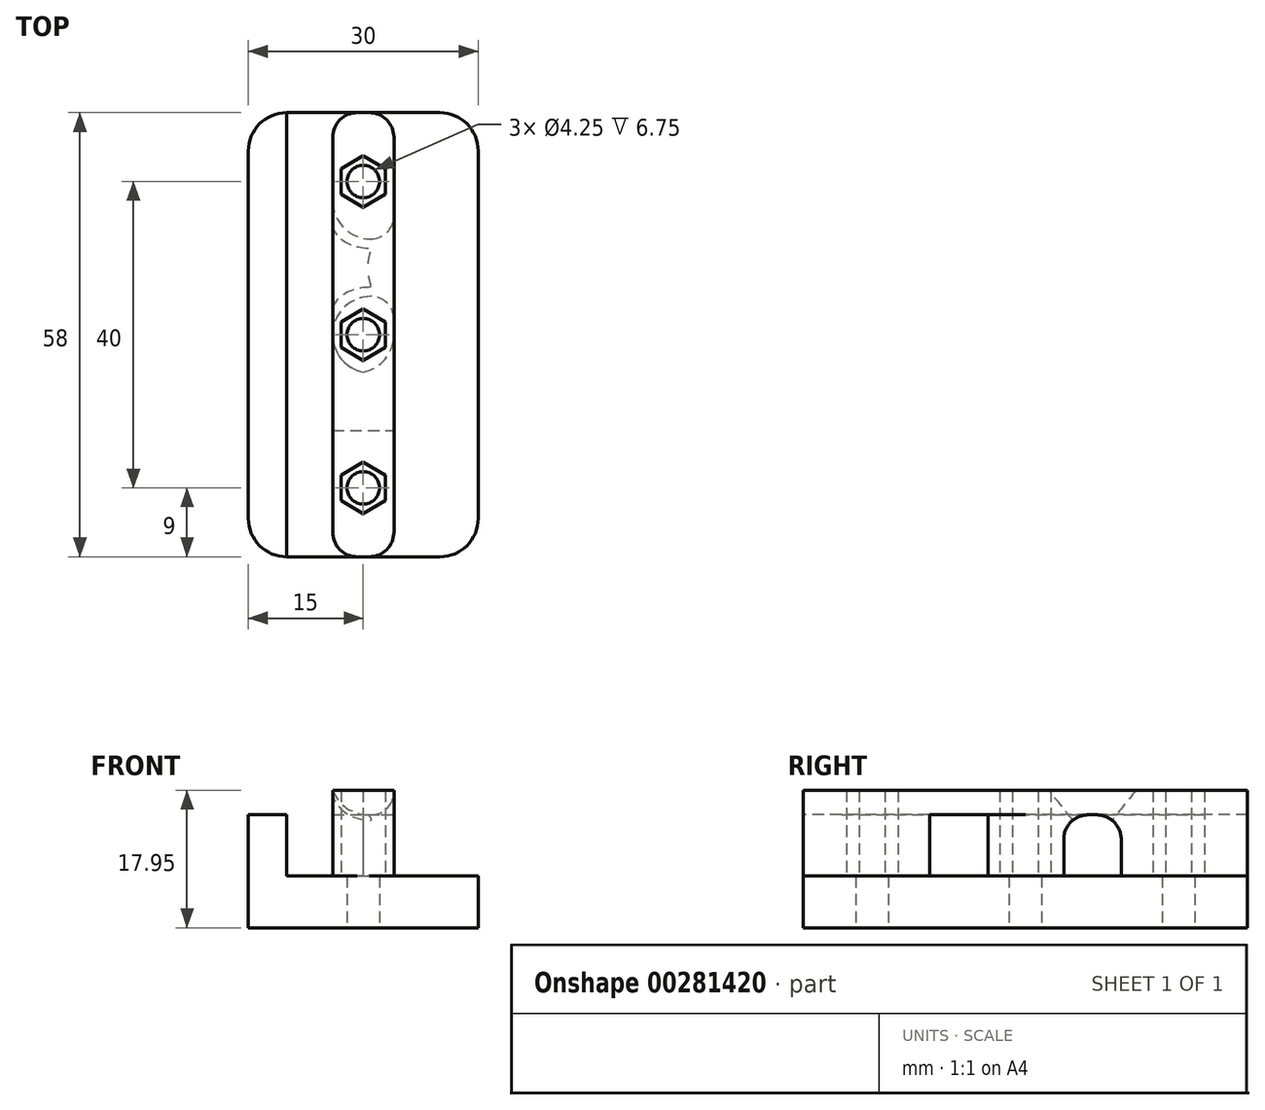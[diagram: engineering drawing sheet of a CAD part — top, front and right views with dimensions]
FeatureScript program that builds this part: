
annotation { "Feature Type Name" : "Feature", "Feature Type Description" : "" }
export const myFeature = defineFeature(function(context is Context, id is Id, definition is map)
    precondition{}
    {
        {
            var Q0;
            Q0=qCreatedBy(makeId("Top.planeOp"),FACE);
            var sketch = newSketch(context, id + "F0", { "sketchPlane" : qUnion([Q0])});
            skLineSegment(sketch, "E0.bottom", {"start": v(15, -29) * mm, "end": v(-15, -29) * mm});
            skLineSegment(sketch, "E0.top", {"start": v(15, 29) * mm, "end": v(-15, 29) * mm});
            skLineSegment(sketch, "E0.left", {"start": v(15, -29) * mm, "end": v(15, 29) * mm});
            skLineSegment(sketch, "E0.right", {"start": v(-15, -29) * mm, "end": v(-15, 29) * mm});
            skPoint(sketch, "E0.middle", {"position": v(0, 0) * mm});
            skCircle(sketch, "E1", {"center": v(0, 20) * mm, "radius": 2.12 * mm});
            skCircle(sketch, "E2", {"center": v(0, -20) * mm, "radius": 2.12 * mm});
            skCircle(sketch, "E3", {"center": v(0, 0) * mm, "radius": 2.12 * mm});
            skSolve(sketch);
        }
        {
            var Q0;
            Q0=qSketchRegion(id+"F0",true);
            extrude(context, id + "F1", {"entities" : qUnion([Q0]), "depth" : 6.75 * mm});
        }
        {
            var Q0;
            Q0=makeQuery(id+"F1.opExtrude","CAP_FACE",FACE,{"disambiguationData":[OSD([sQuery(id+"F0.wireOp",EDGE,"E0.bottom"),sQuery(id+"F0.wireOp",EDGE,"E0.top"),sQuery(id+"F0.wireOp",EDGE,"E0.left"),sQuery(id+"F0.wireOp",EDGE,"E0.right"),sQuery(id+"F0.wireOp",EDGE,"E1"),sQuery(id+"F0.wireOp",EDGE,"KLKllVxa-KRiR-D8UT-5MAC-9W21Uwu7I1FX"),sQuery(id+"F0.wireOp",EDGE,"3S3Oasn0-W67i-79H7-AJHw-8dzInvGUHBWD"),sQuery(id+"F0.wireOp",EDGE,"E2")])],"isStart":false});
            var sketch = newSketch(context, id + "F2", { "sketchPlane" : qUnion([Q0])});
            skLineSegment(sketch, "E4.bottom", {"start": v(-15, 29) * mm, "end": v(-10, 29) * mm});
            skLineSegment(sketch, "E4.top", {"start": v(-15, -29) * mm, "end": v(-10, -29) * mm});
            skLineSegment(sketch, "E4.left", {"start": v(-15, 29) * mm, "end": v(-15, -29) * mm});
            skLineSegment(sketch, "E4.right", {"start": v(-10, 29) * mm, "end": v(-10, -29) * mm});
            skLineSegment(sketch, "E5.bottom", {"start": v(15, 29) * mm, "end": v(10, 29) * mm});
            skLineSegment(sketch, "E5.top", {"start": v(15, -29) * mm, "end": v(10, -29) * mm});
            skLineSegment(sketch, "E5.left", {"start": v(15, 29) * mm, "end": v(15, -29) * mm});
            skLineSegment(sketch, "E5.right", {"start": v(10, 29) * mm, "end": v(10, -29) * mm});
            skLineSegment(sketch, "E6.bottom", {"start": v(4, -29) * mm, "end": v(-4, -29) * mm});
            skLineSegment(sketch, "E6.top", {"start": v(4, 29) * mm, "end": v(-4, 29) * mm});
            skLineSegment(sketch, "E6.left", {"start": v(4, -29) * mm, "end": v(4, -12.5) * mm});
            skLineSegment(sketch, "E6.right", {"start": v(-4, -29) * mm, "end": v(-4, -12.5) * mm});
            skPoint(sketch, "E6.middle", {"position": v(0, 0) * mm});
            skLineSegment(sketch, "E7", {"start": v(-4, 12.5) * mm, "end": v(4, 12.5) * mm});
            skLineSegment(sketch, "E8.MirrorCS", {"start": v(-4, -12.5) * mm, "end": v(4, -12.5) * mm});
            skLineSegment(sketch, "E9.trimOffspring", {"start": v(-4, 12.5) * mm, "end": v(-4, 29) * mm});
            skLineSegment(sketch, "E10.trimOffspring", {"start": v(4, 12.5) * mm, "end": v(4, 29) * mm});
            skPoint(sketch, "E11.visualSharp", {"position": v(-4, 12.5) * mm});
            skLineSegment(sketch, "E11.filletArc", {"start": v(-4, 12.5) * mm, "end": v(-4, 12.5) * mm});
            skPoint(sketch, "E12.visualSharp", {"position": v(4, 12.5) * mm});
            skLineSegment(sketch, "E12.filletArc", {"start": v(4, 12.5) * mm, "end": v(4, 12.5) * mm});
            skPoint(sketch, "E13.visualSharp", {"position": v(-4, -12.5) * mm});
            skLineSegment(sketch, "E13.filletArc", {"start": v(-4, -12.5) * mm, "end": v(-4, -12.5) * mm});
            skPoint(sketch, "E14.visualSharp", {"position": v(4, -12.5) * mm});
            skLineSegment(sketch, "E14.filletArc", {"start": v(4, -12.5) * mm, "end": v(4, -12.5) * mm});
            skPoint(sketch, "E15.visualSharp", {"position": v(-10, 29) * mm});
            skLineSegment(sketch, "E15.filletArc", {"start": v(-10, 29) * mm, "end": v(-10, 29) * mm});
            skPoint(sketch, "E16.visualSharp", {"position": v(-4, 29) * mm});
            skLineSegment(sketch, "E16.filletArc", {"start": v(-4, 29) * mm, "end": v(-4, 29) * mm});
            skPoint(sketch, "E17.visualSharp", {"position": v(4, 29) * mm});
            skLineSegment(sketch, "E17.filletArc", {"start": v(4, 29) * mm, "end": v(4, 29) * mm});
            skPoint(sketch, "E18.visualSharp", {"position": v(10, 29) * mm});
            skLineSegment(sketch, "E18.filletArc", {"start": v(10, 29) * mm, "end": v(10, 29) * mm});
            skPoint(sketch, "E19.visualSharp", {"position": v(10, -29) * mm});
            skLineSegment(sketch, "E19.filletArc", {"start": v(10, -29) * mm, "end": v(10, -29) * mm});
            skPoint(sketch, "E20.visualSharp", {"position": v(4, -29) * mm});
            skLineSegment(sketch, "E20.filletArc", {"start": v(4, -29) * mm, "end": v(4, -29) * mm});
            skPoint(sketch, "E21.visualSharp", {"position": v(-4, -29) * mm});
            skLineSegment(sketch, "E21.filletArc", {"start": v(-4, -29) * mm, "end": v(-4, -29) * mm});
            skPoint(sketch, "E22.visualSharp", {"position": v(-10, -29) * mm});
            skLineSegment(sketch, "E22.filletArc", {"start": v(-10, -29) * mm, "end": v(-10, -29) * mm});
            skCircle(sketch, "E23.cCircle", {"center": v(0, 0) * mm, "radius": 2.9 * mm, "construction": true});
            skLineSegment(sketch, "E23.0", {"start": v(2.9, 1.67) * mm, "end": v(2.9, -1.67) * mm});
            skLineSegment(sketch, "E23.1", {"start": v(2.9, -1.67) * mm, "end": v(0, -3.35) * mm});
            skLineSegment(sketch, "E23.2", {"start": v(0, -3.35) * mm, "end": v(-2.9, -1.67) * mm});
            skLineSegment(sketch, "E23.3", {"start": v(-2.9, -1.67) * mm, "end": v(-2.9, 1.67) * mm});
            skLineSegment(sketch, "E23.4", {"start": v(-2.9, 1.67) * mm, "end": v(0, 3.35) * mm});
            skLineSegment(sketch, "E23.5", {"start": v(0, 3.35) * mm, "end": v(2.9, 1.67) * mm});
            skPoint(sketch, "E23.0.midPoint", {"position": v(2.9, 0) * mm});
            skLineSegment(sketch, "E24.bottom", {"start": v(4, -5) * mm, "end": v(-4, -5) * mm});
            skLineSegment(sketch, "E24.top", {"start": v(4, 5) * mm, "end": v(-4, 5) * mm});
            skLineSegment(sketch, "E24.left", {"start": v(4, -5) * mm, "end": v(4, 5) * mm});
            skLineSegment(sketch, "E24.right", {"start": v(-4, -5) * mm, "end": v(-4, 5) * mm});
            skCircle(sketch, "E25.cCircle", {"center": v(0, -20) * mm, "radius": 2.9 * mm, "construction": true});
            skLineSegment(sketch, "E25.0", {"start": v(2.9, -18.33) * mm, "end": v(2.9, -21.67) * mm});
            skLineSegment(sketch, "E25.1", {"start": v(2.9, -21.67) * mm, "end": v(0, -23.35) * mm});
            skLineSegment(sketch, "E25.2", {"start": v(0, -23.35) * mm, "end": v(-2.9, -21.67) * mm});
            skLineSegment(sketch, "E25.3", {"start": v(-2.9, -21.67) * mm, "end": v(-2.9, -18.33) * mm});
            skLineSegment(sketch, "E25.4", {"start": v(-2.9, -18.33) * mm, "end": v(0, -16.65) * mm});
            skLineSegment(sketch, "E25.5", {"start": v(0, -16.65) * mm, "end": v(2.9, -18.33) * mm});
            skPoint(sketch, "E25.0.midPoint", {"position": v(2.9, -20) * mm});
            skCircle(sketch, "E26.MirrorC", {"center": v(0, 20) * mm, "radius": 2.9 * mm, "construction": true});
            skLineSegment(sketch, "E27.MirrorCS", {"start": v(0, 23.35) * mm, "end": v(-2.9, 21.67) * mm});
            skLineSegment(sketch, "E28.MirrorCS", {"start": v(2.9, 18.33) * mm, "end": v(2.9, 21.67) * mm});
            skLineSegment(sketch, "E29.MirrorCS", {"start": v(-2.9, 21.67) * mm, "end": v(-2.9, 18.33) * mm});
            skLineSegment(sketch, "E30.MirrorCS", {"start": v(2.9, 21.67) * mm, "end": v(0, 23.35) * mm});
            skPoint(sketch, "E31.MirrorP", {"position": v(2.9, 20) * mm});
            skLineSegment(sketch, "E32.MirrorCS", {"start": v(-2.9, 18.33) * mm, "end": v(0, 16.65) * mm});
            skLineSegment(sketch, "E33.MirrorCS", {"start": v(0, 16.65) * mm, "end": v(2.9, 18.33) * mm});
            skPoint(sketch, "E34.visualSharp", {"position": v(-4, 5) * mm});
            skLineSegment(sketch, "E34.filletArc", {"start": v(-4, 5) * mm, "end": v(-4, 5) * mm});
            skPoint(sketch, "E35.visualSharp", {"position": v(4, 5) * mm});
            skLineSegment(sketch, "E35.filletArc", {"start": v(4, 5) * mm, "end": v(4, 5) * mm});
            skPoint(sketch, "E36.visualSharp", {"position": v(4, -5) * mm});
            skLineSegment(sketch, "E36.filletArc", {"start": v(4, -5) * mm, "end": v(4, -5) * mm});
            skPoint(sketch, "E37.visualSharp", {"position": v(-4, -5) * mm});
            skLineSegment(sketch, "E37.filletArc", {"start": v(-4, -5) * mm, "end": v(-4, -5) * mm});
            skSolve(sketch);
        }
        {
            var Q0;
            Q0=qSketchRegion(id+"F2",true);
            extrude(context, id + "F3", {"entities" : qUnion([Q0]), "operationType" : NewBodyOperationType.ADD, "depth" : 8 * mm});
        }
        {
            var Q0;
            Q0=makeQuery(id+"F3.boolean.opBoolean","MERGE",EDGE,{"derivedFrom":[makeQuery(id+"F1.opExtrude","SWEPT_EDGE",EDGE,{"disambiguationData":[OSD([sQuery(id+"F0.wireOp",EDGE,"E0.top"),sQuery(id+"F0.wireOp",EDGE,"E0.left")])]}),makeQuery(id+"F3.opExtrude","SWEPT_EDGE",EDGE,{"disambiguationData":[OSD([sQuery(id+"F2.wireOp",EDGE,"E5.bottom"),sQuery(id+"F2.wireOp",EDGE,"E5.left")])]})]});
            var Q1;
            Q1=makeQuery(id+"F3.boolean.opBoolean","MERGE",EDGE,{"derivedFrom":[makeQuery(id+"F1.opExtrude","SWEPT_EDGE",EDGE,{"disambiguationData":[OSD([sQuery(id+"F0.wireOp",EDGE,"E0.top"),sQuery(id+"F0.wireOp",EDGE,"E0.right")])]}),makeQuery(id+"F3.opExtrude","SWEPT_EDGE",EDGE,{"disambiguationData":[OSD([sQuery(id+"F2.wireOp",EDGE,"E4.bottom"),sQuery(id+"F2.wireOp",EDGE,"E4.left")])]})]});
            var Q2;
            Q2=makeQuery(id+"F3.boolean.opBoolean","MERGE",EDGE,{"derivedFrom":[makeQuery(id+"F1.opExtrude","SWEPT_EDGE",EDGE,{"disambiguationData":[OSD([sQuery(id+"F0.wireOp",EDGE,"E0.bottom"),sQuery(id+"F0.wireOp",EDGE,"E0.right")])]}),makeQuery(id+"F3.opExtrude","SWEPT_EDGE",EDGE,{"disambiguationData":[OSD([sQuery(id+"F2.wireOp",EDGE,"E4.top"),sQuery(id+"F2.wireOp",EDGE,"E4.left")])]})]});
            var Q3;
            Q3=makeQuery(id+"F3.boolean.opBoolean","MERGE",EDGE,{"derivedFrom":[makeQuery(id+"F1.opExtrude","SWEPT_EDGE",EDGE,{"disambiguationData":[OSD([sQuery(id+"F0.wireOp",EDGE,"E0.bottom"),sQuery(id+"F0.wireOp",EDGE,"E0.left")])]}),makeQuery(id+"F3.opExtrude","SWEPT_EDGE",EDGE,{"disambiguationData":[OSD([sQuery(id+"F2.wireOp",EDGE,"E5.top"),sQuery(id+"F2.wireOp",EDGE,"E5.left")])]})]});
            fillet(context, id + "F4", {"entities" : qUnion([Q0, Q1, Q2, Q3]), "radius" : 5 * mm, "tangentPropagation" : true, "allowEdgeOverflow" : false});
        }
        {
            var Q0;
            Q0=makeQuery(id+"F3.opExtrude","CAP_FACE",FACE,{"disambiguationData":[OSD([sQuery(id+"F2.wireOp",EDGE,"E6.top"),sQuery(id+"F2.wireOp",EDGE,"E7"),sQuery(id+"F2.wireOp",EDGE,"E9.trimOffspring"),sQuery(id+"F2.wireOp",EDGE,"E10.trimOffspring"),sQuery(id+"F2.wireOp",EDGE,"E11.filletArc"),sQuery(id+"F2.wireOp",EDGE,"E12.filletArc"),sQuery(id+"F2.wireOp",EDGE,"E16.filletArc"),sQuery(id+"F2.wireOp",EDGE,"E17.filletArc"),sQuery(id+"F2.wireOp",EDGE,"E27.MirrorCS"),sQuery(id+"F2.wireOp",EDGE,"E28.MirrorCS"),sQuery(id+"F2.wireOp",EDGE,"E29.MirrorCS"),sQuery(id+"F2.wireOp",EDGE,"E30.MirrorCS"),sQuery(id+"F2.wireOp",EDGE,"E32.MirrorCS"),sQuery(id+"F2.wireOp",EDGE,"E33.MirrorCS")])],"isStart":false});
            var sketch = newSketch(context, id + "F5", { "sketchPlane" : qUnion([Q0])});
            skLineSegment(sketch, "E38.bottom", {"start": v(4, 29) * mm, "end": v(-4, 29) * mm});
            skLineSegment(sketch, "E38.top", {"start": v(4, -29) * mm, "end": v(-4, -29) * mm});
            skLineSegment(sketch, "E38.left", {"start": v(4, 29) * mm, "end": v(4, -29) * mm});
            skLineSegment(sketch, "E38.right", {"start": v(-4, 29) * mm, "end": v(-4, -29) * mm});
            skPoint(sketch, "E38.middle", {"position": v(0, 0) * mm});
            skPoint(sketch, "E39.visualSharp", {"position": v(-4, 29) * mm});
            skLineSegment(sketch, "E39.filletArc", {"start": v(-4, 29) * mm, "end": v(-4, 29) * mm});
            skPoint(sketch, "E40.visualSharp", {"position": v(4, 29) * mm});
            skLineSegment(sketch, "E40.filletArc", {"start": v(4, 29) * mm, "end": v(4, 29) * mm});
            skPoint(sketch, "E41.visualSharp", {"position": v(-4, -29) * mm});
            skLineSegment(sketch, "E41.filletArc", {"start": v(-4, -29) * mm, "end": v(-4, -29) * mm});
            skPoint(sketch, "E42.visualSharp", {"position": v(4, -29) * mm});
            skLineSegment(sketch, "E42.filletArc", {"start": v(4, -29) * mm, "end": v(4, -29) * mm});
            skCircle(sketch, "E43.cCircle", {"center": v(0, -20) * mm, "radius": 2.9 * mm, "construction": true});
            skLineSegment(sketch, "E43.0", {"start": v(2.9, -18.33) * mm, "end": v(2.9, -21.67) * mm});
            skLineSegment(sketch, "E43.1", {"start": v(2.9, -21.67) * mm, "end": v(0, -23.35) * mm});
            skLineSegment(sketch, "E43.2", {"start": v(0, -23.35) * mm, "end": v(-2.9, -21.67) * mm});
            skLineSegment(sketch, "E43.3", {"start": v(-2.9, -21.67) * mm, "end": v(-2.9, -18.33) * mm});
            skLineSegment(sketch, "E43.4", {"start": v(-2.9, -18.33) * mm, "end": v(0, -16.65) * mm});
            skLineSegment(sketch, "E43.5", {"start": v(0, -16.65) * mm, "end": v(2.9, -18.33) * mm});
            skPoint(sketch, "E43.0.midPoint", {"position": v(2.9, -20) * mm});
            skLineSegment(sketch, "E44.0.1.0", {"start": v(-2.9, -1.67) * mm, "end": v(-2.9, 1.67) * mm});
            skPoint(sketch, "E44.0.1.1", {"position": v(2.9, 0) * mm});
            skLineSegment(sketch, "E44.0.1.2", {"start": v(0, -3.35) * mm, "end": v(-2.9, -1.67) * mm});
            skCircle(sketch, "E44.0.1.3", {"center": v(0, 0) * mm, "radius": 2.9 * mm, "construction": true});
            skLineSegment(sketch, "E44.0.1.4", {"start": v(2.9, 1.67) * mm, "end": v(2.9, -1.67) * mm});
            skLineSegment(sketch, "E44.0.1.5", {"start": v(2.9, -1.67) * mm, "end": v(0, -3.35) * mm});
            skLineSegment(sketch, "E44.0.1.6", {"start": v(0, 3.35) * mm, "end": v(2.9, 1.67) * mm});
            skLineSegment(sketch, "E44.0.1.7", {"start": v(-2.9, 1.67) * mm, "end": v(0, 3.35) * mm});
            skLineSegment(sketch, "E44.0.2.0", {"start": v(-2.9, 18.33) * mm, "end": v(-2.9, 21.67) * mm});
            skPoint(sketch, "E44.0.2.1", {"position": v(2.9, 20) * mm});
            skLineSegment(sketch, "E44.0.2.2", {"start": v(0, 16.65) * mm, "end": v(-2.9, 18.33) * mm});
            skCircle(sketch, "E44.0.2.3", {"center": v(0, 20) * mm, "radius": 2.9 * mm, "construction": true});
            skLineSegment(sketch, "E44.0.2.4", {"start": v(2.9, 21.67) * mm, "end": v(2.9, 18.33) * mm});
            skLineSegment(sketch, "E44.0.2.5", {"start": v(2.9, 18.33) * mm, "end": v(0, 16.65) * mm});
            skLineSegment(sketch, "E44.0.2.6", {"start": v(0, 23.35) * mm, "end": v(2.9, 21.67) * mm});
            skLineSegment(sketch, "E44.0.2.7", {"start": v(-2.9, 21.67) * mm, "end": v(0, 23.35) * mm});
            skLineSegment(sketch, "E44.direction1", {"start": v(-2.9, -21.67) * mm, "end": v(22.1, -21.67) * mm, "construction": true});
            skLineSegment(sketch, "E44.direction2", {"start": v(-2.9, -21.67) * mm, "end": v(-2.9, -1.67) * mm, "construction": true});
            skSolve(sketch);
        }
        {
            var Q0;
            Q0=qSketchRegion(id+"F5",true);
            extrude(context, id + "F6", {"entities" : qUnion([Q0]), "operationType" : NewBodyOperationType.ADD, "depth" : 3.2 * mm});
        }
        {
            var Q0;
            Q0=makeQuery(id+"F6.boolean.opBoolean","MERGE",EDGE,{"derivedFrom":[makeQuery(id+"F3.opExtrude","SWEPT_EDGE",EDGE,{"disambiguationData":[OSD([sQuery(id+"F0.wireOp",EDGE,"E0.top"),sQuery(id+"F2.wireOp",EDGE,"E6.top"),sQuery(id+"F2.wireOp",EDGE,"E9.trimOffspring")])]}),makeQuery(id+"F6.opExtrude","SWEPT_EDGE",EDGE,{"disambiguationData":[OSD([sQuery(id+"F5.wireOp",EDGE,"E38.bottom"),sQuery(id+"F5.wireOp",EDGE,"E38.right")])]})]});
            var Q1;
            Q1=makeQuery(id+"F6.boolean.opBoolean","MERGE",EDGE,{"derivedFrom":[makeQuery(id+"F3.opExtrude","SWEPT_EDGE",EDGE,{"disambiguationData":[OSD([sQuery(id+"F0.wireOp",EDGE,"E0.top"),sQuery(id+"F2.wireOp",EDGE,"E6.top"),sQuery(id+"F2.wireOp",EDGE,"E10.trimOffspring")])]}),makeQuery(id+"F6.opExtrude","SWEPT_EDGE",EDGE,{"disambiguationData":[OSD([sQuery(id+"F5.wireOp",EDGE,"E38.bottom"),sQuery(id+"F5.wireOp",EDGE,"E38.left")])]})]});
            var Q2;
            Q2=makeQuery(id+"F6.boolean.opBoolean","MERGE",EDGE,{"derivedFrom":[makeQuery(id+"F3.opExtrude","SWEPT_EDGE",EDGE,{"disambiguationData":[OSD([sQuery(id+"F0.wireOp",EDGE,"E0.bottom"),sQuery(id+"F2.wireOp",EDGE,"E6.bottom"),sQuery(id+"F2.wireOp",EDGE,"E6.right")])]}),makeQuery(id+"F6.opExtrude","SWEPT_EDGE",EDGE,{"disambiguationData":[OSD([sQuery(id+"F5.wireOp",EDGE,"E38.top"),sQuery(id+"F5.wireOp",EDGE,"E38.right")])]})]});
            var Q3;
            Q3=makeQuery(id+"F6.boolean.opBoolean","MERGE",EDGE,{"derivedFrom":[makeQuery(id+"F3.opExtrude","SWEPT_EDGE",EDGE,{"disambiguationData":[OSD([sQuery(id+"F0.wireOp",EDGE,"E0.bottom"),sQuery(id+"F2.wireOp",EDGE,"E6.bottom"),sQuery(id+"F2.wireOp",EDGE,"E6.left")])]}),makeQuery(id+"F6.opExtrude","SWEPT_EDGE",EDGE,{"disambiguationData":[OSD([sQuery(id+"F5.wireOp",EDGE,"E38.top"),sQuery(id+"F5.wireOp",EDGE,"E38.left")])]})]});
            var Q4;
            Q4=makeQuery(id+"F3.opExtrude","CAP_EDGE",EDGE,{"disambiguationData":[OSD([sQuery(id+"F2.wireOp",EDGE,"E24.bottom")])],"isStart":false});
            var Q5;
            Q5=makeQuery(id+"F3.opExtrude","CAP_EDGE",EDGE,{"disambiguationData":[OSD([sQuery(id+"F2.wireOp",EDGE,"E24.top")])],"isStart":false});
            var Q6;
            Q6=makeQuery(id+"F3.opExtrude","CAP_EDGE",EDGE,{"disambiguationData":[OSD([sQuery(id+"F2.wireOp",EDGE,"E7")])],"isStart":false});
            var Q7;
            Q7=makeQuery(id+"F3.opExtrude","CAP_EDGE",EDGE,{"disambiguationData":[OSD([sQuery(id+"F2.wireOp",EDGE,"E8.MirrorCS")])],"isStart":false});
            fillet(context, id + "F7", {"entities" : qUnion([Q0, Q1, Q2, Q3, Q4, Q5, Q6, Q7]), "radius" : 3.2 * mm, "tangentPropagation" : true, "allowEdgeOverflow" : false});
        }
        {
            var Q0;
            Q0=makeQuery(id+"F3.opExtrude","SWEPT_EDGE",EDGE,{"disambiguationData":[OSD([sQuery(id+"F2.wireOp",EDGE,"E7"),sQuery(id+"F2.wireOp",EDGE,"E9.trimOffspring")])]});
            var Q1;
            Q1=makeQuery(id+"F3.opExtrude","SWEPT_EDGE",EDGE,{"disambiguationData":[OSD([sQuery(id+"F2.wireOp",EDGE,"E24.bottom"),sQuery(id+"F2.wireOp",EDGE,"E24.right")])]});
            var Q2;
            Q2=makeQuery(id+"F3.opExtrude","SWEPT_EDGE",EDGE,{"disambiguationData":[OSD([sQuery(id+"F2.wireOp",EDGE,"E24.bottom"),sQuery(id+"F2.wireOp",EDGE,"E24.left")])]});
            fillet(context, id + "F8", {"entities" : qUnion([Q0, Q1, Q2]), "radius" : 5 * mm, "tangentPropagation" : true, "allowEdgeOverflow" : false});
        }
        {
            var Q0;
            Q0=makeQuery(id+"F3.opExtrude","CAP_FACE",FACE,{"disambiguationData":[OSD([sQuery(id+"F2.wireOp",EDGE,"E5.bottom"),sQuery(id+"F2.wireOp",EDGE,"E5.top"),sQuery(id+"F2.wireOp",EDGE,"E5.left"),sQuery(id+"F2.wireOp",EDGE,"E5.right")])],"isStart":false});
            var sketch = newSketch(context, id + "F9", { "sketchPlane" : qUnion([Q0])});
            skLineSegment(sketch, "E45.bottom", {"start": v(7.5, -32.86) * mm, "end": v(18.84, -32.86) * mm});
            skLineSegment(sketch, "E45.top", {"start": v(7.5, 31.16) * mm, "end": v(18.84, 31.16) * mm});
            skLineSegment(sketch, "E45.left", {"start": v(7.5, -32.86) * mm, "end": v(7.5, 31.16) * mm});
            skLineSegment(sketch, "E45.right", {"start": v(18.84, -32.86) * mm, "end": v(18.84, 31.16) * mm});
            skLineSegment(sketch, "E46.bottom", {"start": v(-5.8, -32.3) * mm, "end": v(-21.39, -32.3) * mm});
            skLineSegment(sketch, "E46.top", {"start": v(-5.8, 31.16) * mm, "end": v(-21.39, 31.16) * mm});
            skLineSegment(sketch, "E46.left", {"start": v(-5.8, -32.3) * mm, "end": v(-5.8, 31.16) * mm});
            skLineSegment(sketch, "E46.right", {"start": v(-21.39, -32.3) * mm, "end": v(-21.39, 31.16) * mm});
            skSolve(sketch);
        }
        {
            var Q0;
            Q0=makeQuery(id+"F9.imprint","IMPRINT",FACE,{"disambiguationData":[TD([[makeQuery(id+"F9.imprint","IMPRINT",EDGE,{"derivedFrom":sQuery(id+"F9.wireOp",EDGE,"E45.bottom")}),1.0]])]});
            var Q1;
            {var subQ0=sQuery(id+"F2.wireOp",EDGE,"E5.right");Q1=makeQuery(id+"F9.imprint","IMPRINT",FACE,{"disambiguationData":[TD([[makeQuery(id+"F9.imprint","IMPRINT",EDGE,{"derivedFrom":makeQuery(id+"F3.opExtrude","CAP_EDGE",EDGE,{"disambiguationData":[OSD([subQ0])],"isStart":false})}),1.0]])]});}
            extrude(context, id + "F10", {"entities" : qUnion([Q0, Q1]), "operationType" : NewBodyOperationType.REMOVE, "oppositeDirection" : true, "depth" : 8 * mm});
        }
        {
            var Q0;
            Q0=makeQuery(id+"F3.opExtrude","SWEPT_EDGE",EDGE,{"disambiguationData":[OSD([sQuery(id+"F2.wireOp",EDGE,"E7"),sQuery(id+"F2.wireOp",EDGE,"E10.trimOffspring")])]});
            fillet(context, id + "F11", {"entities" : qUnion([Q0]), "radius" : 3 * mm, "tangentPropagation" : true, "allowEdgeOverflow" : false});
        }
    });
